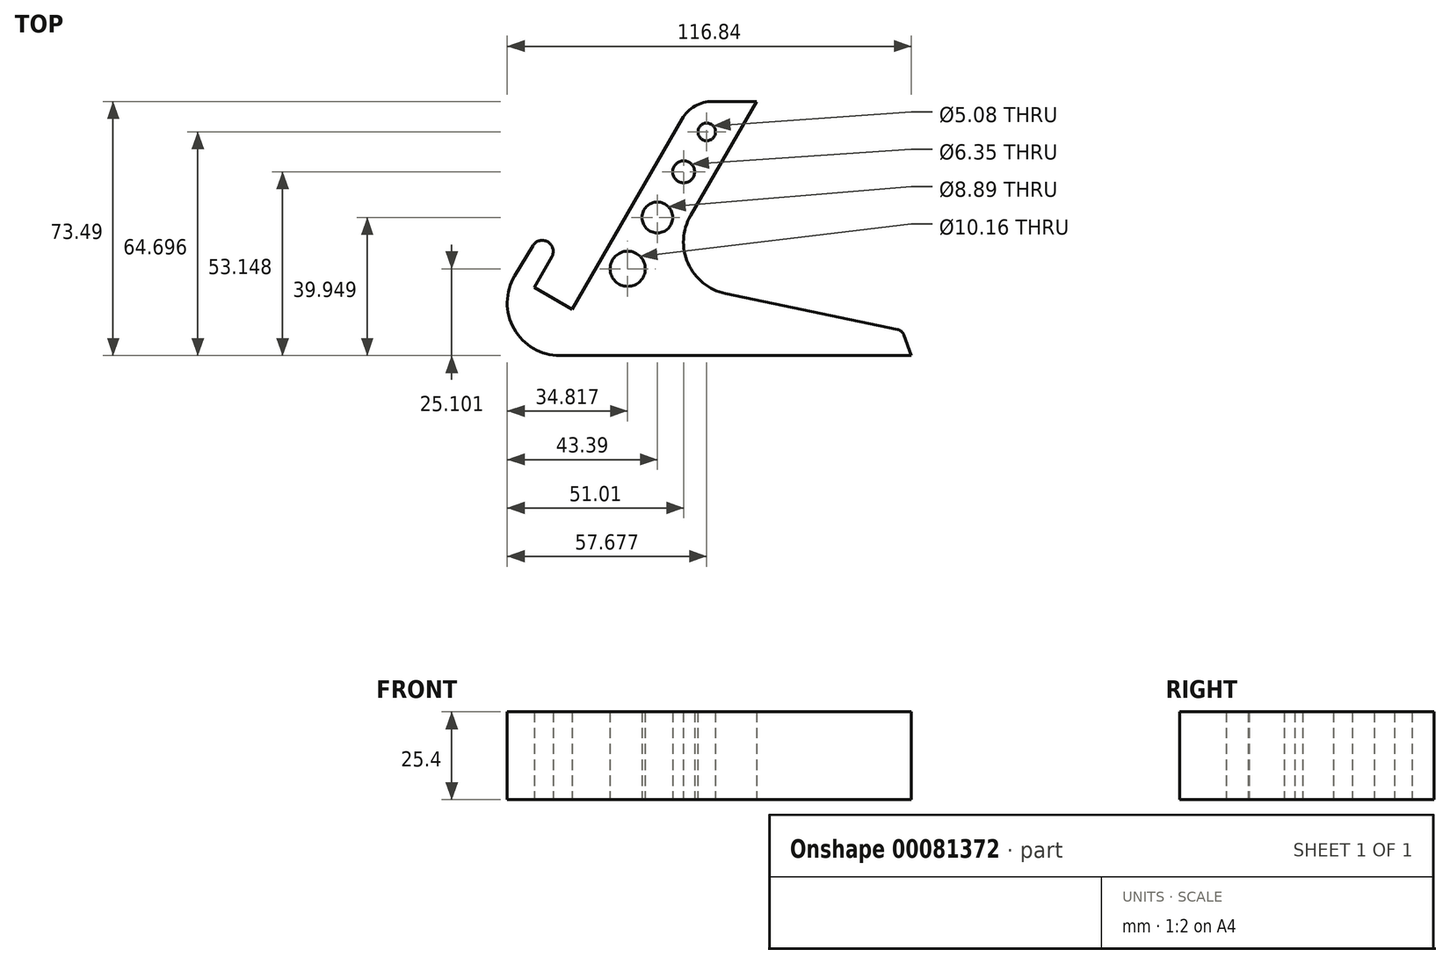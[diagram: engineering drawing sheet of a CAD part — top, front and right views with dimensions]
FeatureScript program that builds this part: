
annotation { "Feature Type Name" : "Feature", "Feature Type Description" : "" }
export const myFeature = defineFeature(function(context is Context, id is Id, definition is map)
    precondition{}
    {
        {
            var Q0;
            Q0=qCreatedBy(makeId("Top.planeOp"),FACE);
            var sketch = newSketch(context, id + "F0", { "sketchPlane" : qUnion([Q0])});
            skLineSegment(sketch, "E0", {"start": v(-56.8, 0) * mm, "end": v(44.8, 0) * mm});
            skArc(sketch, "E1", {"start": v(-69.87, 23.08) * mm, "mid": v(-70.06, 7.73) * mm, "end": v(-56.8, 0) * mm});
            skLineSegment(sketch, "E2", {"start": v(-69.87, 23.08) * mm, "end": v(-64.64, 31.8) * mm});
            skArc(sketch, "E3", {"start": v(-59.17, 28.57) * mm, "mid": v(-60.3, 32.9) * mm, "end": v(-64.64, 31.8) * mm});
            skLineSegment(sketch, "E4", {"start": v(-53.25, 13.42) * mm, "end": v(-21.5, 68.41) * mm});
            skLineSegment(sketch, "E5", {"start": v(-12.7, 73.5) * mm, "end": v(0, 73.5) * mm});
            skLineSegment(sketch, "E6", {"start": v(0, 73.5) * mm, "end": v(-19.05, 40.5) * mm});
            skLineSegment(sketch, "E7", {"start": v(-8.96, 17.96) * mm, "end": v(40.76, 7.58) * mm});
            skLineSegment(sketch, "E8", {"start": v(42.63, 5.97) * mm, "end": v(44.8, 0) * mm});
            skArc(sketch, "E9.filletArc", {"start": v(42.63, 5.97) * mm, "mid": v(41.9, 7.02) * mm, "end": v(40.76, 7.58) * mm});
            skPoint(sketch, "E10.visualSharp", {"position": v(-18.57, 73.5) * mm});
            skArc(sketch, "E10.filletArc", {"start": v(-12.7, 73.5) * mm, "mid": v(-17.78, 72.13) * mm, "end": v(-21.5, 68.41) * mm});
            skLineSegment(sketch, "E11", {"start": v(-59.17, 28.57) * mm, "end": v(-64.25, 19.77) * mm});
            skLineSegment(sketch, "E12", {"start": v(-64.25, 19.77) * mm, "end": v(-53.25, 13.42) * mm});
            skArc(sketch, "E13", {"start": v(-19.05, 40.5) * mm, "mid": v(-19.76, 26.65) * mm, "end": v(-8.96, 17.96) * mm});
            skLineSegment(sketch, "E14", {"start": v(0, 73.5) * mm, "end": v(0, 0) * mm, "construction": true});
            skLineSegment(sketch, "E15", {"start": v(-36.9, 41.74) * mm, "end": v(-27.61, 41.74) * mm, "construction": true});
            skLineSegment(sketch, "E16", {"start": v(-9.28, 73.5) * mm, "end": v(-13.1, 66.9) * mm, "construction": true});
            skCircle(sketch, "E17", {"center": v(-14.36, 64.7) * mm, "radius": 2.54 * mm});
            skCircle(sketch, "E18", {"center": v(-21.03, 53.15) * mm, "radius": 3.18 * mm});
            skCircle(sketch, "E19", {"center": v(-28.65, 39.95) * mm, "radius": 4.45 * mm});
            skCircle(sketch, "E20", {"center": v(-37.22, 25.1) * mm, "radius": 5.08 * mm});
            skLineSegment(sketch, "E21.trimOffspring", {"start": v(-15.63, 62.5) * mm, "end": v(-19.44, 55.9) * mm, "construction": true});
            skLineSegment(sketch, "E22.trimOffspring", {"start": v(-22.62, 50.4) * mm, "end": v(-26.43, 43.8) * mm, "construction": true});
            skLineSegment(sketch, "E23.trimOffspring", {"start": v(-30.87, 36.1) * mm, "end": v(-34.68, 29.5) * mm, "construction": true});
            skLineSegment(sketch, "E24.trimOffspring", {"start": v(-39.76, 20.7) * mm, "end": v(-45.94, 10) * mm, "construction": true});
            skSolve(sketch);
        }
        {
            var Q0;
            Q0=makeQuery(id+"F0.imprint","IMPRINT",FACE,{"disambiguationData":[TD([[makeQuery(id+"F0.imprint","IMPRINT",EDGE,{"derivedFrom":sQuery(id+"F0.wireOp",EDGE,"E0")}),1.0]])]});
            extrude(context, id + "F1", {"entities" : qUnion([Q0]), "depth" : 25.4 * mm});
        }
    });
